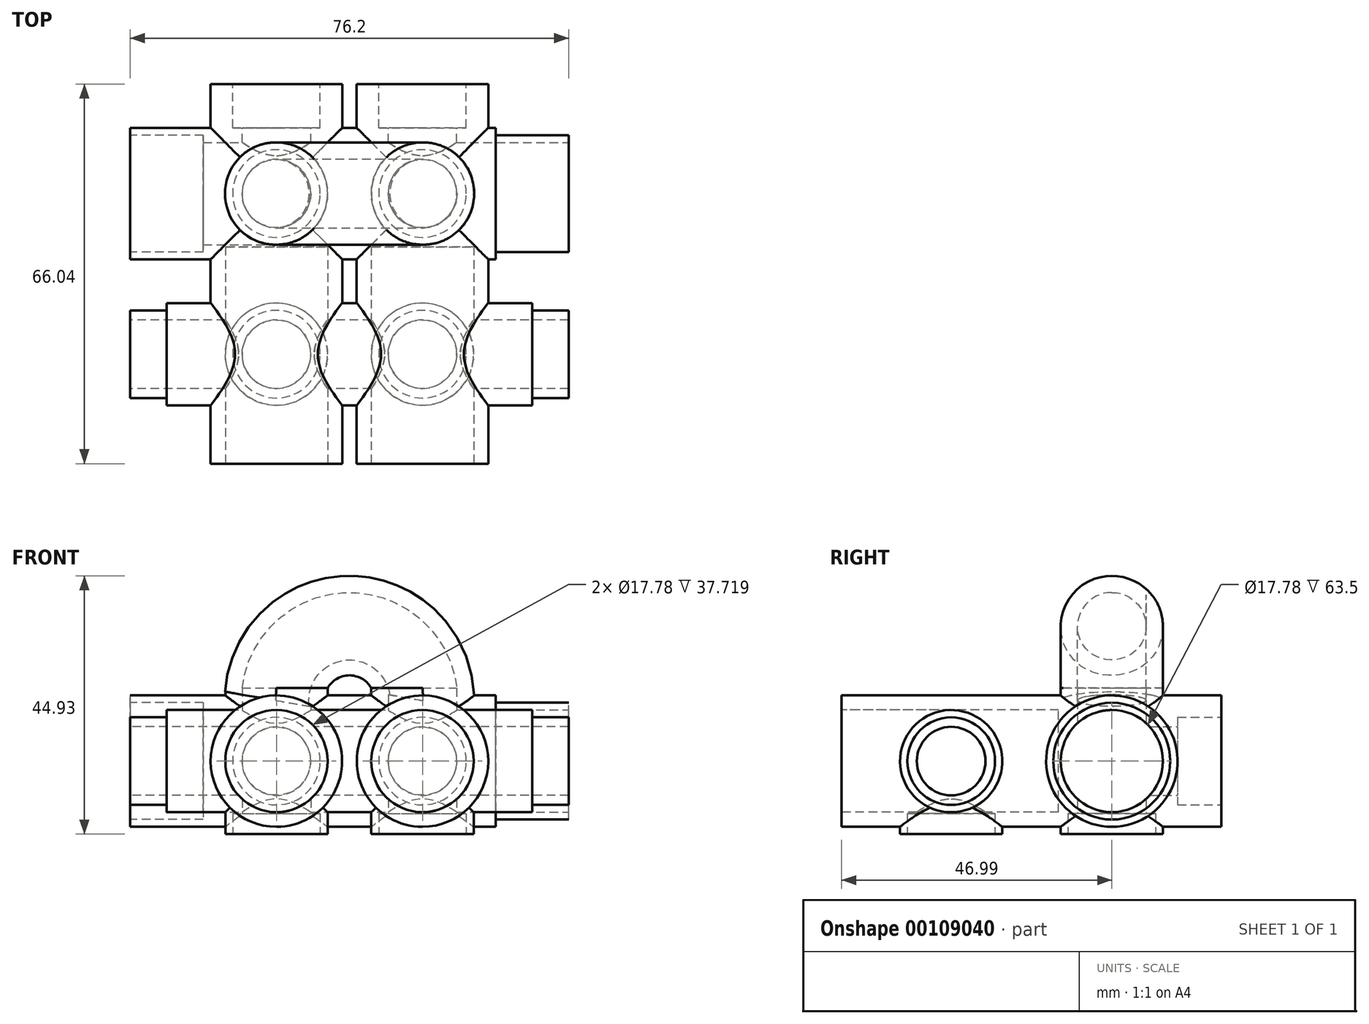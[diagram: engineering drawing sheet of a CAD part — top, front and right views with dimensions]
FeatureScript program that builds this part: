
annotation { "Feature Type Name" : "Feature", "Feature Type Description" : "" }
export const myFeature = defineFeature(function(context is Context, id is Id, definition is map)
    precondition{}
    {
        {
            var Q0;
            Q0=qCreatedBy(makeId("Top.planeOp"),FACE);
            var sketch = newSketch(context, id + "F0", { "sketchPlane" : qUnion([Q0])});
            skCircle(sketch, "E0", {"center": v(0, 0) * mm, "radius": 5.97 * mm});
            skCircle(sketch, "E1", {"center": v(0, 0) * mm, "radius": 8.9 * mm});
            skLineSegment(sketch, "E2", {"start": v(0, 0) * mm, "end": v(-25.4, 0) * mm});
            skCircle(sketch, "E3", {"center": v(-25.4, 0) * mm, "radius": 5.97 * mm});
            skCircle(sketch, "E4", {"center": v(-25.4, 0) * mm, "radius": 8.9 * mm});
            skSolve(sketch);
        }
        {
            var Q0;
            Q0=qCreatedBy(makeId("Front.planeOp"),FACE);
            var sketch = newSketch(context, id + "F1", { "sketchPlane" : qUnion([Q0])});
            skCircle(sketch, "E5", {"center": v(0, 0) * mm, "radius": 5.97 * mm});
            skCircle(sketch, "E6", {"center": v(0, 0) * mm, "radius": 11.43 * mm});
            skLineSegment(sketch, "E7", {"start": v(0, 0) * mm, "end": v(-25.4, 0) * mm});
            skCircle(sketch, "E8", {"center": v(-25.4, 0) * mm, "radius": 5.97 * mm});
            skCircle(sketch, "E9", {"center": v(-25.4, 0) * mm, "radius": 11.43 * mm});
            skSolve(sketch);
        }
        {
            var Q0;
            Q0=qCreatedBy(makeId("Right.planeOp"),FACE);
            var sketch = newSketch(context, id + "F2", { "sketchPlane" : qUnion([Q0])});
            skCircle(sketch, "E10", {"center": v(0, 0) * mm, "radius": 5.97 * mm});
            skCircle(sketch, "E11", {"center": v(0, 0) * mm, "radius": 8.9 * mm});
            skSolve(sketch);
        }
        {
            var Q0;
            Q0=qCreatedBy(makeId("Right.planeOp"),FACE);
            var sketch = newSketch(context, id + "F3", { "sketchPlane" : qUnion([Q0])});
            skLineSegment(sketch, "E12", {"start": v(0, 0) * mm, "end": v(0, -12.7) * mm});
            skLineSegment(sketch, "E13", {"start": v(0, 0) * mm, "end": v(27.94, 0) * mm});
            skCircle(sketch, "E14", {"center": v(27.94, 0) * mm, "radius": 8.9 * mm});
            skCircle(sketch, "E15", {"center": v(27.94, 0) * mm, "radius": 11.43 * mm});
            skLineSegment(sketch, "E16", {"start": v(27.94, 0) * mm, "end": v(27.94, -12.7) * mm});
            skLineSegment(sketch, "E17", {"start": v(27.94, 0) * mm, "end": v(47, 0) * mm});
            skLineSegment(sketch, "E18", {"start": v(0, 0) * mm, "end": v(-25.4, 0) * mm});
            skSolve(sketch);
        }
        {
            var Q0;
            Q0=qCreatedBy(makeId("Top.planeOp"),FACE);
            var sketch = newSketch(context, id + "F4", { "sketchPlane" : qUnion([Q0])});
            skCircle(sketch, "E19", {"center": v(0, 27.94) * mm, "radius": 8.9 * mm});
            skCircle(sketch, "E20", {"center": v(0, 27.94) * mm, "radius": 5.97 * mm});
            skLineSegment(sketch, "E21", {"start": v(0, 0) * mm, "end": v(0, 27.94) * mm});
            skLineSegment(sketch, "E22", {"start": v(0, 27.94) * mm, "end": v(-25.4, 27.94) * mm});
            skCircle(sketch, "E23", {"center": v(-25.4, 27.94) * mm, "radius": 5.97 * mm});
            skCircle(sketch, "E24", {"center": v(-25.4, 27.94) * mm, "radius": 8.9 * mm});
            skSolve(sketch);
        }
        {
            var Q0;
            Q0=makeQuery(id+"F0.imprint","IMPRINT",FACE,{"disambiguationData":[TD([[makeQuery(id+"F0.imprint","IMPRINT",EDGE,{"derivedFrom":sQuery(id+"F0.wireOp",EDGE,"E0")}),-1.0]])]});
            var Q1;
            Q1=makeQuery(id+"F0.imprint","IMPRINT",FACE,{"disambiguationData":[TD([[makeQuery(id+"F0.imprint","IMPRINT",EDGE,{"derivedFrom":sQuery(id+"F0.wireOp",EDGE,"E3")}),-1.0]])]});
            var Q2;
            Q2=sQuery(id+"F3.wireOp",EDGE,"E12");
            var Q3;
            Q3=sQuery(id+"F3.wireOp",EDGE,"4cSytoO9-y9dV-aX7s-iAXl-VCevQILe5KTB");
            sweep(context, id + "F5", {"profiles" : qUnion([Q0, Q1]), "path" : qUnion([Q2, Q3])});
        }
        {
            var Q0;
            Q0=makeQuery(id+"F4.imprint","IMPRINT",FACE,{"disambiguationData":[TD([[makeQuery(id+"F4.imprint","IMPRINT",EDGE,{"derivedFrom":sQuery(id+"F4.wireOp",EDGE,"E23")}),-1.0]])]});
            var Q1;
            {var subQ0=sQuery(id+"F4.wireOp",EDGE,"E21");var subQ1=sQuery(id+"F4.wireOp",EDGE,"E19");var subQ2=makeQuery(id+"F4.imprint","INTERSECT",VERTEX,{"derivedFrom":[subQ1,subQ0]});Q1=makeQuery(id+"F4.imprint","IMPRINT",FACE,{"disambiguationData":[TD([[makeQuery(id+"F4.imprint","IMPRINT",EDGE,{"disambiguationData":[TD([[subQ2,1.0]])],"derivedFrom":subQ1}),1.0]])]});}
            var Q2;
            {var subQ0=sQuery(id+"F4.wireOp",EDGE,"E21");var subQ1=sQuery(id+"F4.wireOp",EDGE,"E19");var subQ2=makeQuery(id+"F4.imprint","INTERSECT",VERTEX,{"derivedFrom":[subQ1,subQ0]});Q2=makeQuery(id+"F4.imprint","IMPRINT",FACE,{"disambiguationData":[TD([[makeQuery(id+"F4.imprint","IMPRINT",EDGE,{"disambiguationData":[TD([[subQ2,-1.0]])],"derivedFrom":subQ1}),1.0]])]});}
            var Q3;
            Q3=sQuery(id+"F3.wireOp",EDGE,"E16");
            sweep(context, id + "F6", {"profiles" : qUnion([Q0, Q1, Q2]), "path" : qUnion([Q3])});
        }
        {
            var Q0;
            Q0=makeQuery(id+"F1.imprint","IMPRINT",FACE,{"disambiguationData":[TD([[makeQuery(id+"F1.imprint","IMPRINT",EDGE,{"derivedFrom":sQuery(id+"F1.wireOp",EDGE,"E8")}),-1.0]])]});
            var Q1;
            Q1=makeQuery(id+"F1.imprint","IMPRINT",FACE,{"disambiguationData":[TD([[makeQuery(id+"F1.imprint","IMPRINT",EDGE,{"derivedFrom":sQuery(id+"F1.wireOp",EDGE,"E5")}),-1.0]])]});
            var Q2;
            Q2=sQuery(id+"F3.wireOp",EDGE,"E13");
            var Q3;
            Q3=sQuery(id+"F3.wireOp",EDGE,"E17");
            sweep(context, id + "F7", {"operationType" : NewBodyOperationType.ADD, "profiles" : qUnion([Q0, Q1]), "path" : qUnion([Q2, Q3])});
        }
        {
            var Q0;
            {var subQ0=sQuery(id+"F3.wireOp",EDGE,"E15");var subQ1=sQuery(id+"F3.wireOp",EDGE,"E13");var subQ2=makeQuery(id+"F3.imprint","INTERSECT",VERTEX,{"derivedFrom":[subQ1,subQ0]});Q0=makeQuery(id+"F3.imprint","IMPRINT",FACE,{"disambiguationData":[TD([[makeQuery(id+"F3.imprint","IMPRINT",EDGE,{"disambiguationData":[TD([[subQ2,-1.0]])],"derivedFrom":subQ1}),1.0]])]});}
            var Q1;
            {var subQ0=sQuery(id+"F3.wireOp",EDGE,"E17");var subQ1=sQuery(id+"F3.wireOp",EDGE,"E14");var subQ2=makeQuery(id+"F3.imprint","INTERSECT",VERTEX,{"derivedFrom":[subQ1,subQ0]});Q1=makeQuery(id+"F3.imprint","IMPRINT",FACE,{"disambiguationData":[TD([[makeQuery(id+"F3.imprint","IMPRINT",EDGE,{"disambiguationData":[TD([[subQ2,1.0]])],"derivedFrom":subQ1}),-1.0]])]});}
            var Q2;
            {var subQ0=sQuery(id+"F3.wireOp",EDGE,"E15");var subQ1=sQuery(id+"F3.wireOp",EDGE,"E13");var subQ2=makeQuery(id+"F3.imprint","INTERSECT",VERTEX,{"derivedFrom":[subQ1,subQ0]});Q2=makeQuery(id+"F3.imprint","IMPRINT",FACE,{"disambiguationData":[TD([[makeQuery(id+"F3.imprint","IMPRINT",EDGE,{"disambiguationData":[TD([[subQ2,-1.0]])],"derivedFrom":subQ1}),-1.0]])]});}
            extrude(context, id + "F8", {"entities" : qUnion([Q0, Q1, Q2]), "depth" : 12.7 * mm, "hasSecondDirection" : true, "secondDirectionOppositeDirection" : true, "secondDirectionDepth" : 50.8 * mm});
        }
        {
            var Q0;
            Q0=makeQuery(id+"F2.imprint","IMPRINT",FACE,{"disambiguationData":[TD([[makeQuery(id+"F2.imprint","IMPRINT",EDGE,{"derivedFrom":sQuery(id+"F2.wireOp",EDGE,"E10")}),-1.0]])]});
            extrude(context, id + "F9", {"entities" : qUnion([Q0]), "operationType" : NewBodyOperationType.ADD, "depth" : 25.4 * mm, "hasSecondDirection" : true, "secondDirectionOppositeDirection" : true, "secondDirectionDepth" : 50.8 * mm});
        }
        {
            var Q0;
            Q0=makeQuery(id+"F0.imprint","IMPRINT",FACE,{"disambiguationData":[TD([[makeQuery(id+"F0.imprint","IMPRINT",EDGE,{"derivedFrom":sQuery(id+"F0.wireOp",EDGE,"E0")}),1.0]])]});
            var Q1;
            Q1=makeQuery(id+"F0.imprint","IMPRINT",FACE,{"disambiguationData":[TD([[makeQuery(id+"F0.imprint","IMPRINT",EDGE,{"derivedFrom":sQuery(id+"F0.wireOp",EDGE,"E3")}),1.0]])]});
            extrude(context, id + "F10", {"entities" : qUnion([Q0, Q1]), "operationType" : NewBodyOperationType.REMOVE, "oppositeDirection" : true, "depth" : 25.4 * mm});
        }
        {
            var Q0;
            Q0=makeQuery(id+"F1.imprint","IMPRINT",FACE,{"disambiguationData":[TD([[makeQuery(id+"F1.imprint","IMPRINT",EDGE,{"derivedFrom":sQuery(id+"F1.wireOp",EDGE,"E8")}),-1.0]])]});
            var Q1;
            Q1=makeQuery(id+"F1.imprint","IMPRINT",FACE,{"disambiguationData":[TD([[makeQuery(id+"F1.imprint","IMPRINT",EDGE,{"derivedFrom":sQuery(id+"F1.wireOp",EDGE,"E5")}),-1.0]])]});
            extrude(context, id + "F11", {"entities" : qUnion([Q0, Q1]), "operationType" : NewBodyOperationType.ADD, "depth" : 19.05 * mm});
        }
        {
            var Q0;
            Q0=makeQuery(id+"F2.imprint","IMPRINT",FACE,{"disambiguationData":[TD([[makeQuery(id+"F2.imprint","IMPRINT",EDGE,{"derivedFrom":sQuery(id+"F2.wireOp",EDGE,"E10")}),1.0]])]});
            extrude(context, id + "F12", {"entities" : qUnion([Q0]), "operationType" : NewBodyOperationType.REMOVE, "depth" : 25.4 * mm, "hasSecondDirection" : true, "secondDirectionOppositeDirection" : true, "secondDirectionDepth" : 50.8 * mm});
        }
        {
            var Q0;
            Q0=makeQuery(id+"F0.imprint","IMPRINT",FACE,{"disambiguationData":[TD([[makeQuery(id+"F0.imprint","IMPRINT",EDGE,{"derivedFrom":sQuery(id+"F0.wireOp",EDGE,"E0")}),1.0]])]});
            var Q1;
            Q1=makeQuery(id+"F0.imprint","IMPRINT",FACE,{"disambiguationData":[TD([[makeQuery(id+"F0.imprint","IMPRINT",EDGE,{"derivedFrom":sQuery(id+"F0.wireOp",EDGE,"E3")}),1.0]])]});
            extrude(context, id + "F13", {"entities" : qUnion([Q0, Q1]), "operationType" : NewBodyOperationType.REMOVE, "oppositeDirection" : true, "depth" : 25.4 * mm});
        }
        {
            var Q0;
            Q0=makeQuery(id+"F1.imprint","IMPRINT",FACE,{"disambiguationData":[TD([[makeQuery(id+"F1.imprint","IMPRINT",EDGE,{"derivedFrom":sQuery(id+"F1.wireOp",EDGE,"E5")}),1.0]])]});
            var Q1;
            Q1=makeQuery(id+"F1.imprint","IMPRINT",FACE,{"disambiguationData":[TD([[makeQuery(id+"F1.imprint","IMPRINT",EDGE,{"derivedFrom":sQuery(id+"F1.wireOp",EDGE,"E8")}),1.0]])]});
            extrude(context, id + "F14", {"entities" : qUnion([Q0, Q1]), "operationType" : NewBodyOperationType.REMOVE, "depth" : 25.4 * mm, "hasSecondDirection" : true, "secondDirectionOppositeDirection" : true, "secondDirectionDepth" : 18.67 * mm});
        }
        {
            var Q0;
            Q0=makeQuery(id+"F7.opSweep","CAP_FACE",FACE,{"disambiguationData":[OSD([sQuery(id+"F1.wireOp",EDGE,"E5"),sQuery(id+"F1.wireOp",EDGE,"E6"),sQuery(id+"F3.wireOp",VERTEX,"E17.end")])],"isStart":false});
            var sketch = newSketch(context, id + "F15", { "sketchPlane" : qUnion([Q0])});
            skCircle(sketch, "E25", {"center": v(0, 0) * mm, "radius": 5.97 * mm});
            skCircle(sketch, "E26", {"center": v(25.4, 0) * mm, "radius": 5.97 * mm});
            skSolve(sketch);
        }
        {
            var Q0;
            Q0=makeQuery(id+"F15.imprint","IMPRINT",FACE,{"disambiguationData":[TD([[makeQuery(id+"F15.imprint","IMPRINT",EDGE,{"derivedFrom":sQuery(id+"F15.wireOp",EDGE,"E25")}),-1.0]])]});
            var Q1;
            Q1=makeQuery(id+"F15.imprint","IMPRINT",FACE,{"disambiguationData":[TD([[makeQuery(id+"F15.imprint","IMPRINT",EDGE,{"derivedFrom":sQuery(id+"F15.wireOp",EDGE,"E26")}),1.0]])]});
            extrude(context, id + "F16", {"entities" : qUnion([Q0, Q1]), "operationType" : NewBodyOperationType.REMOVE, "oppositeDirection" : true, "depth" : 25.4 * mm});
        }
        {
            var Q0;
            Q0=makeQuery(id+"F8.opExtrude","CAP_FACE",FACE,{"disambiguationData":[OSD([sQuery(id+"F3.wireOp",EDGE,"E14"),sQuery(id+"F3.wireOp",EDGE,"E15")])],"isStart":false});
            var sketch = newSketch(context, id + "F17", { "sketchPlane" : qUnion([Q0])});
            skCircle(sketch, "E27", {"center": v(27.94, 0) * mm, "radius": 8.9 * mm});
            skSolve(sketch);
        }
        {
            var Q0;
            Q0=makeQuery(id+"F17.imprint","IMPRINT",FACE,{"disambiguationData":[TD([[makeQuery(id+"F17.imprint","IMPRINT",EDGE,{"derivedFrom":sQuery(id+"F17.wireOp",EDGE,"E27")}),1.0]])]});
            extrude(context, id + "F18", {"entities" : qUnion([Q0]), "operationType" : NewBodyOperationType.REMOVE, "oppositeDirection" : true, "depth" : 53.6 * mm});
        }
        {
            var Q0;
            Q0=makeQuery(id+"F4.imprint","IMPRINT",FACE,{"disambiguationData":[TD([[makeQuery(id+"F4.imprint","IMPRINT",EDGE,{"derivedFrom":sQuery(id+"F4.wireOp",EDGE,"E23")}),1.0]])]});
            var Q1;
            {var subQ0=sQuery(id+"F4.wireOp",EDGE,"E21");var subQ1=sQuery(id+"F4.wireOp",EDGE,"E20");var subQ2=makeQuery(id+"F4.imprint","INTERSECT",VERTEX,{"derivedFrom":[subQ1,subQ0]});Q1=makeQuery(id+"F4.imprint","IMPRINT",FACE,{"disambiguationData":[TD([[makeQuery(id+"F4.imprint","IMPRINT",EDGE,{"disambiguationData":[TD([[subQ2,-1.0]])],"derivedFrom":subQ1}),1.0]])]});}
            extrude(context, id + "F19", {"entities" : qUnion([Q0, Q1]), "operationType" : NewBodyOperationType.REMOVE, "oppositeDirection" : true, "depth" : 25.4 * mm});
        }
        {
            var Q0;
            Q0=makeQuery(id+"F11.opExtrude","CAP_FACE",FACE,{"disambiguationData":[OSD([sQuery(id+"F1.wireOp",EDGE,"E8"),sQuery(id+"F1.wireOp",EDGE,"E9")])],"isStart":false});
            var sketch = newSketch(context, id + "F20", { "sketchPlane" : qUnion([Q0])});
            skCircle(sketch, "E28", {"center": v(-25.4, 0) * mm, "radius": 8.9 * mm});
            skCircle(sketch, "E29", {"center": v(0, 0) * mm, "radius": 8.9 * mm});
            skCircle(sketch, "E30", {"center": v(0, 0) * mm, "radius": 5.97 * mm});
            skSolve(sketch);
        }
        {
            var Q0;
            Q0=makeQuery(id+"F20.imprint","IMPRINT",FACE,{"disambiguationData":[TD([[makeQuery(id+"F20.imprint","IMPRINT",EDGE,{"derivedFrom":sQuery(id+"F20.wireOp",EDGE,"E28")}),1.0]])]});
            var Q1;
            Q1=makeQuery(id+"F20.imprint","IMPRINT",FACE,{"disambiguationData":[TD([[makeQuery(id+"F20.imprint","IMPRINT",EDGE,{"derivedFrom":sQuery(id+"F20.wireOp",EDGE,"E29")}),1.0]])]});
            extrude(context, id + "F21", {"entities" : qUnion([Q0, Q1]), "operationType" : NewBodyOperationType.REMOVE, "oppositeDirection" : true, "depth" : 37.72 * mm});
        }
        {
            var Q0;
            Q0=makeQuery(id+"F9.opExtrude","CAP_FACE",FACE,{"disambiguationData":[OSD([sQuery(id+"F2.wireOp",EDGE,"E10"),sQuery(id+"F2.wireOp",EDGE,"E11")])],"isStart":false});
            var sketch = newSketch(context, id + "F22", { "sketchPlane" : qUnion([Q0])});
            skCircle(sketch, "E31", {"center": v(0, 0) * mm, "radius": 7.62 * mm});
            skSolve(sketch);
        }
        {
            var Q0;
            Q0=makeQuery(id+"F22.imprint","IMPRINT",FACE,{"disambiguationData":[TD([[makeQuery(id+"F22.imprint","IMPRINT",EDGE,{"derivedFrom":sQuery(id+"F22.wireOp",EDGE,"E31")}),-1.0]])]});
            extrude(context, id + "F23", {"entities" : qUnion([Q0]), "operationType" : NewBodyOperationType.REMOVE, "oppositeDirection" : true, "depth" : 6.35 * mm});
        }
        {
            var Q0;
            Q0=makeQuery(id+"F9.opExtrude","CAP_FACE",FACE,{"disambiguationData":[OSD([sQuery(id+"F2.wireOp",EDGE,"E10"),sQuery(id+"F2.wireOp",EDGE,"E11")])],"isStart":true});
            var sketch = newSketch(context, id + "F24", { "sketchPlane" : qUnion([Q0])});
            skCircle(sketch, "E32", {"center": v(0, 0) * mm, "radius": 7.62 * mm});
            skSolve(sketch);
        }
        {
            var Q0;
            Q0=makeQuery(id+"F24.imprint","IMPRINT",FACE,{"disambiguationData":[TD([[makeQuery(id+"F24.imprint","IMPRINT",EDGE,{"derivedFrom":sQuery(id+"F24.wireOp",EDGE,"E32")}),-1.0]])]});
            extrude(context, id + "F25", {"entities" : qUnion([Q0]), "operationType" : NewBodyOperationType.REMOVE, "oppositeDirection" : true, "depth" : 6.35 * mm});
        }
        {
            var Q0;
            Q0=makeQuery(id+"F4.imprint","IMPRINT",FACE,{"disambiguationData":[TD([[makeQuery(id+"F4.imprint","IMPRINT",EDGE,{"derivedFrom":sQuery(id+"F4.wireOp",EDGE,"E23")}),-1.0]])]});
            var Q1;
            {var subQ0=sQuery(id+"F4.wireOp",EDGE,"E21");var subQ1=sQuery(id+"F4.wireOp",EDGE,"E19");var subQ2=makeQuery(id+"F4.imprint","INTERSECT",VERTEX,{"derivedFrom":[subQ1,subQ0]});Q1=makeQuery(id+"F4.imprint","IMPRINT",FACE,{"disambiguationData":[TD([[makeQuery(id+"F4.imprint","IMPRINT",EDGE,{"disambiguationData":[TD([[subQ2,1.0]])],"derivedFrom":subQ1}),1.0]])]});}
            var Q2;
            {var subQ0=sQuery(id+"F4.wireOp",EDGE,"E21");var subQ1=sQuery(id+"F4.wireOp",EDGE,"E19");var subQ2=makeQuery(id+"F4.imprint","INTERSECT",VERTEX,{"derivedFrom":[subQ1,subQ0]});Q2=makeQuery(id+"F4.imprint","IMPRINT",FACE,{"disambiguationData":[TD([[makeQuery(id+"F4.imprint","IMPRINT",EDGE,{"disambiguationData":[TD([[subQ2,-1.0]])],"derivedFrom":subQ1}),1.0]])]});}
            extrude(context, id + "F26", {"entities" : qUnion([Q0, Q1, Q2]), "depth" : 12.7 * mm});
        }
        {
            var Q0;
            Q0=makeQuery(id+"F17.imprint","IMPRINT",FACE,{"disambiguationData":[TD([[makeQuery(id+"F17.imprint","IMPRINT",EDGE,{"derivedFrom":sQuery(id+"F17.wireOp",EDGE,"E27")}),1.0]])]});
            extrude(context, id + "F27", {"entities" : qUnion([Q0]), "operationType" : NewBodyOperationType.REMOVE, "oppositeDirection" : true, "depth" : 71.04 * mm});
        }
        {
            var Q0;
            Q0=makeQuery(id+"F4.imprint","IMPRINT",FACE,{"disambiguationData":[TD([[makeQuery(id+"F4.imprint","IMPRINT",EDGE,{"derivedFrom":sQuery(id+"F4.wireOp",EDGE,"E23")}),1.0]])]});
            extrude(context, id + "F28", {"entities" : qUnion([Q0]), "operationType" : NewBodyOperationType.REMOVE, "depth" : 25.4 * mm});
        }
        {
            var Q0;
            {var subQ0=sQuery(id+"F4.wireOp",EDGE,"E21");var subQ1=sQuery(id+"F4.wireOp",EDGE,"E20");var subQ2=makeQuery(id+"F4.imprint","INTERSECT",VERTEX,{"derivedFrom":[subQ1,subQ0]});Q0=makeQuery(id+"F4.imprint","IMPRINT",FACE,{"disambiguationData":[TD([[makeQuery(id+"F4.imprint","IMPRINT",EDGE,{"disambiguationData":[TD([[subQ2,-1.0]])],"derivedFrom":subQ1}),1.0]])]});}
            var Q1;
            {var subQ0=sQuery(id+"F4.wireOp",EDGE,"E21");var subQ1=sQuery(id+"F4.wireOp",EDGE,"E20");var subQ2=makeQuery(id+"F4.imprint","INTERSECT",VERTEX,{"derivedFrom":[subQ1,subQ0]});Q1=makeQuery(id+"F4.imprint","IMPRINT",FACE,{"disambiguationData":[TD([[makeQuery(id+"F4.imprint","IMPRINT",EDGE,{"disambiguationData":[TD([[subQ2,1.0]])],"derivedFrom":subQ1}),1.0]])]});}
            extrude(context, id + "F29", {"entities" : qUnion([Q0, Q1]), "operationType" : NewBodyOperationType.REMOVE, "depth" : 25.4 * mm});
        }
        {
            var Q0;
            {var subQ0=sQuery(id+"F4.wireOp",EDGE,"E21");var subQ1=sQuery(id+"F4.wireOp",EDGE,"E20");var subQ2=makeQuery(id+"F4.imprint","INTERSECT",VERTEX,{"derivedFrom":[subQ1,subQ0]});Q0=makeQuery(id+"F4.imprint","IMPRINT",FACE,{"disambiguationData":[TD([[makeQuery(id+"F4.imprint","IMPRINT",EDGE,{"disambiguationData":[TD([[subQ2,1.0]])],"derivedFrom":subQ1}),1.0]])]});}
            var Q1;
            {var subQ0=sQuery(id+"F4.wireOp",EDGE,"E21");var subQ1=sQuery(id+"F4.wireOp",EDGE,"E20");var subQ2=makeQuery(id+"F4.imprint","INTERSECT",VERTEX,{"derivedFrom":[subQ1,subQ0]});Q1=makeQuery(id+"F4.imprint","IMPRINT",FACE,{"disambiguationData":[TD([[makeQuery(id+"F4.imprint","IMPRINT",EDGE,{"disambiguationData":[TD([[subQ2,-1.0]])],"derivedFrom":subQ1}),1.0]])]});}
            extrude(context, id + "F30", {"entities" : qUnion([Q0, Q1]), "operationType" : NewBodyOperationType.REMOVE, "oppositeDirection" : true, "depth" : 25.4 * mm});
        }
        {
            var Q0;
            Q0=makeQuery(id+"F15.imprint","IMPRINT",FACE,{"disambiguationData":[TD([[makeQuery(id+"F15.imprint","IMPRINT",EDGE,{"derivedFrom":sQuery(id+"F15.wireOp",EDGE,"E25")}),-1.0]])]});
            var Q1;
            Q1=makeQuery(id+"F15.imprint","IMPRINT",FACE,{"disambiguationData":[TD([[makeQuery(id+"F15.imprint","IMPRINT",EDGE,{"derivedFrom":sQuery(id+"F15.wireOp",EDGE,"E26")}),1.0]])]});
            extrude(context, id + "F31", {"entities" : qUnion([Q0, Q1]), "operationType" : NewBodyOperationType.REMOVE, "oppositeDirection" : true, "depth" : 25.4 * mm});
        }
        {
            var Q0;
            Q0=makeQuery(id+"F5.opSweep","CAP_FACE",FACE,{"disambiguationData":[OSD([sQuery(id+"F0.wireOp",EDGE,"E0"),sQuery(id+"F0.wireOp",EDGE,"E1"),sQuery(id+"F3.wireOp",VERTEX,"E12.end")])],"isStart":false});
            var sketch = newSketch(context, id + "F32", { "sketchPlane" : qUnion([Q0])});
            skCircle(sketch, "E33", {"center": v(0, 0) * mm, "radius": 7.62 * mm});
            skSolve(sketch);
        }
        {
            var Q0;
            Q0=makeQuery(id+"F5.opSweep","CAP_FACE",FACE,{"disambiguationData":[OSD([sQuery(id+"F0.wireOp",EDGE,"E3"),sQuery(id+"F0.wireOp",EDGE,"E4"),sQuery(id+"F3.wireOp",VERTEX,"E12.end")])],"isStart":false});
            var sketch = newSketch(context, id + "F33", { "sketchPlane" : qUnion([Q0])});
            skCircle(sketch, "E34", {"center": v(-25.4, 0) * mm, "radius": 7.62 * mm});
            skSolve(sketch);
        }
        {
            var Q0;
            Q0=makeQuery(id+"F6.opSweep","CAP_FACE",FACE,{"disambiguationData":[OSD([sQuery(id+"F3.wireOp",VERTEX,"E16.end"),sQuery(id+"F4.wireOp",EDGE,"E23"),sQuery(id+"F4.wireOp",EDGE,"E24")])],"isStart":false});
            var sketch = newSketch(context, id + "F34", { "sketchPlane" : qUnion([Q0])});
            skCircle(sketch, "E35", {"center": v(-25.4, -27.94) * mm, "radius": 7.62 * mm});
            skSolve(sketch);
        }
        {
            var Q0;
            Q0=makeQuery(id+"F6.opSweep","CAP_FACE",FACE,{"disambiguationData":[OSD([sQuery(id+"F3.wireOp",VERTEX,"E16.end"),sQuery(id+"F4.wireOp",EDGE,"E19"),sQuery(id+"F4.wireOp",EDGE,"E20")])],"isStart":false});
            var sketch = newSketch(context, id + "F35", { "sketchPlane" : qUnion([Q0])});
            skCircle(sketch, "E36", {"center": v(0, -27.94) * mm, "radius": 7.62 * mm});
            skSolve(sketch);
        }
        {
            var Q0;
            Q0=makeQuery(id+"F33.imprint","IMPRINT",FACE,{"disambiguationData":[TD([[makeQuery(id+"F33.imprint","IMPRINT",EDGE,{"derivedFrom":sQuery(id+"F33.wireOp",EDGE,"E34")}),1.0]])]});
            extrude(context, id + "F36", {"entities" : qUnion([Q0]), "operationType" : NewBodyOperationType.REMOVE, "oppositeDirection" : true, "depth" : 3.56 * mm});
        }
        {
            var Q0;
            Q0=makeQuery(id+"F32.imprint","IMPRINT",FACE,{"disambiguationData":[TD([[makeQuery(id+"F32.imprint","IMPRINT",EDGE,{"derivedFrom":sQuery(id+"F32.wireOp",EDGE,"E33")}),1.0]])]});
            extrude(context, id + "F37", {"entities" : qUnion([Q0]), "operationType" : NewBodyOperationType.REMOVE, "oppositeDirection" : true, "depth" : 3.56 * mm});
        }
        {
            var Q0;
            Q0=makeQuery(id+"F35.imprint","IMPRINT",FACE,{"disambiguationData":[TD([[makeQuery(id+"F35.imprint","IMPRINT",EDGE,{"derivedFrom":sQuery(id+"F35.wireOp",EDGE,"E36")}),1.0]])]});
            extrude(context, id + "F38", {"entities" : qUnion([Q0]), "operationType" : NewBodyOperationType.REMOVE, "oppositeDirection" : true, "depth" : 3.56 * mm});
        }
        {
            var Q0;
            Q0=makeQuery(id+"F34.imprint","IMPRINT",FACE,{"disambiguationData":[TD([[makeQuery(id+"F34.imprint","IMPRINT",EDGE,{"derivedFrom":sQuery(id+"F34.wireOp",EDGE,"E35")}),1.0]])]});
            extrude(context, id + "F39", {"entities" : qUnion([Q0]), "operationType" : NewBodyOperationType.REMOVE, "oppositeDirection" : true, "depth" : 3.56 * mm});
        }
        {
            var Q0;
            Q0=makeQuery(id+"F26.opExtrude","CAP_FACE",FACE,{"disambiguationData":[OSD([sQuery(id+"F4.wireOp",EDGE,"E23"),sQuery(id+"F4.wireOp",EDGE,"E24")])],"isStart":false});
            var sketch = newSketch(context, id + "F40", { "sketchPlane" : qUnion([Q0])});
            skCircle(sketch, "E37", {"center": v(-25.4, 27.94) * mm, "radius": 7.62 * mm});
            skSolve(sketch);
        }
        {
            var Q0;
            Q0=makeQuery(id+"F26.opExtrude","CAP_FACE",FACE,{"disambiguationData":[OSD([sQuery(id+"F4.wireOp",EDGE,"E19"),sQuery(id+"F4.wireOp",EDGE,"E20")])],"isStart":false});
            var sketch = newSketch(context, id + "F41", { "sketchPlane" : qUnion([Q0])});
            skCircle(sketch, "E38", {"center": v(0, 27.94) * mm, "radius": 7.62 * mm});
            skSolve(sketch);
        }
        {
            var Q0;
            Q0=qCreatedBy(makeId("Front.planeOp"),FACE);
            cPlane(context, id + "F42", {"entities" : qUnion([Q0]), "cplaneType" : CPlaneType.OFFSET, "offset" : 27.94 * mm, "oppositeDirection" : true, "width" : 152.4 * mm, "height" : 152.4 * mm});
        }
        {
            var Q0;
            Q0=qCreatedBy(id+"F42.planeOp",FACE);
            var sketch = newSketch(context, id + "F43", { "sketchPlane" : qUnion([Q0])});
            skLineSegment(sketch, "E39", {"start": v(0, 0) * mm, "end": v(0, 10.54) * mm});
            skArc(sketch, "E40", {"start": v(0, 10.54) * mm, "mid": v(-12.7, 23.24) * mm, "end": v(-25.4, 10.54) * mm});
            skLineSegment(sketch, "E41", {"start": v(-25.4, 0) * mm, "end": v(-25.4, 10.54) * mm});
            skLineSegment(sketch, "E42", {"start": v(0, 0) * mm, "end": v(-25.4, 0) * mm});
            skSolve(sketch);
        }
        {
            var Q0;
            Q0=makeQuery(id+"F26.opExtrude","CAP_FACE",FACE,{"disambiguationData":[OSD([sQuery(id+"F4.wireOp",EDGE,"E19"),sQuery(id+"F4.wireOp",EDGE,"E20")])],"isStart":false});
            var Q1;
            Q1=sQuery(id+"F43.wireOp",EDGE,"E40");
            sweep(context, id + "F44", {"operationType" : NewBodyOperationType.ADD, "profiles" : qUnion([Q0]), "path" : qUnion([Q1])});
        }
        {
            var Q0;
            Q0=makeQuery(id+"F7.opSweep","CAP_FACE",FACE,{"disambiguationData":[OSD([sQuery(id+"F1.wireOp",EDGE,"E5"),sQuery(id+"F1.wireOp",EDGE,"E6"),sQuery(id+"F3.wireOp",VERTEX,"E17.end")])],"isStart":false});
            var sketch = newSketch(context, id + "F45", { "sketchPlane" : qUnion([Q0])});
            skCircle(sketch, "E43", {"center": v(0, 0) * mm, "radius": 7.62 * mm});
            skCircle(sketch, "E44", {"center": v(25.4, 0) * mm, "radius": 7.62 * mm});
            skLineSegment(sketch, "E45", {"start": v(0, 0) * mm, "end": v(25.4, 0) * mm});
            skSolve(sketch);
        }
        {
            var Q0;
            Q0=makeQuery(id+"F45.imprint","IMPRINT",FACE,{"disambiguationData":[TD([[makeQuery(id+"F45.imprint","IMPRINT",EDGE,{"derivedFrom":sQuery(id+"F45.wireOp",EDGE,"E43")}),1.0]])]});
            extrude(context, id + "F46", {"entities" : qUnion([Q0]), "operationType" : NewBodyOperationType.REMOVE, "oppositeDirection" : true, "depth" : 7.62 * mm});
        }
        {
            var Q0;
            Q0=makeQuery(id+"F45.imprint","IMPRINT",FACE,{"disambiguationData":[TD([[makeQuery(id+"F45.imprint","IMPRINT",EDGE,{"derivedFrom":sQuery(id+"F45.wireOp",EDGE,"E44")}),1.0]])]});
            extrude(context, id + "F47", {"entities" : qUnion([Q0]), "operationType" : NewBodyOperationType.REMOVE, "oppositeDirection" : true, "depth" : 7.62 * mm});
        }
        {
            var Q0;
            Q0=makeQuery(id+"F8.opExtrude","CAP_FACE",FACE,{"disambiguationData":[OSD([sQuery(id+"F3.wireOp",EDGE,"E14"),sQuery(id+"F3.wireOp",EDGE,"E15")])],"isStart":true});
            var sketch = newSketch(context, id + "F48", { "sketchPlane" : qUnion([Q0])});
            skCircle(sketch, "E46", {"center": v(-27.94, 0) * mm, "radius": 10.16 * mm});
            skSolve(sketch);
        }
        {
            var Q0;
            Q0=makeQuery(id+"F48.imprint","IMPRINT",FACE,{"disambiguationData":[TD([[makeQuery(id+"F48.imprint","IMPRINT",EDGE,{"derivedFrom":sQuery(id+"F48.wireOp",EDGE,"E46")}),1.0]])]});
            extrude(context, id + "F49", {"entities" : qUnion([Q0]), "operationType" : NewBodyOperationType.REMOVE, "oppositeDirection" : true, "depth" : 12.7 * mm});
        }
        {
            var Q0;
            Q0=makeQuery(id+"F8.opExtrude","CAP_FACE",FACE,{"disambiguationData":[OSD([sQuery(id+"F3.wireOp",EDGE,"E14"),sQuery(id+"F3.wireOp",EDGE,"E15")])],"isStart":false});
            var sketch = newSketch(context, id + "F50", { "sketchPlane" : qUnion([Q0])});
            skCircle(sketch, "E47", {"center": v(27.94, 0) * mm, "radius": 10.16 * mm});
            skSolve(sketch);
        }
        {
            var Q0;
            Q0=makeQuery(id+"F50.imprint","IMPRINT",FACE,{"disambiguationData":[TD([[makeQuery(id+"F50.imprint","IMPRINT",EDGE,{"derivedFrom":sQuery(id+"F50.wireOp",EDGE,"E47")}),1.0]])]});
            extrude(context, id + "F51", {"entities" : qUnion([Q0]), "operationType" : NewBodyOperationType.ADD, "depth" : 12.7 * mm});
        }
    });
